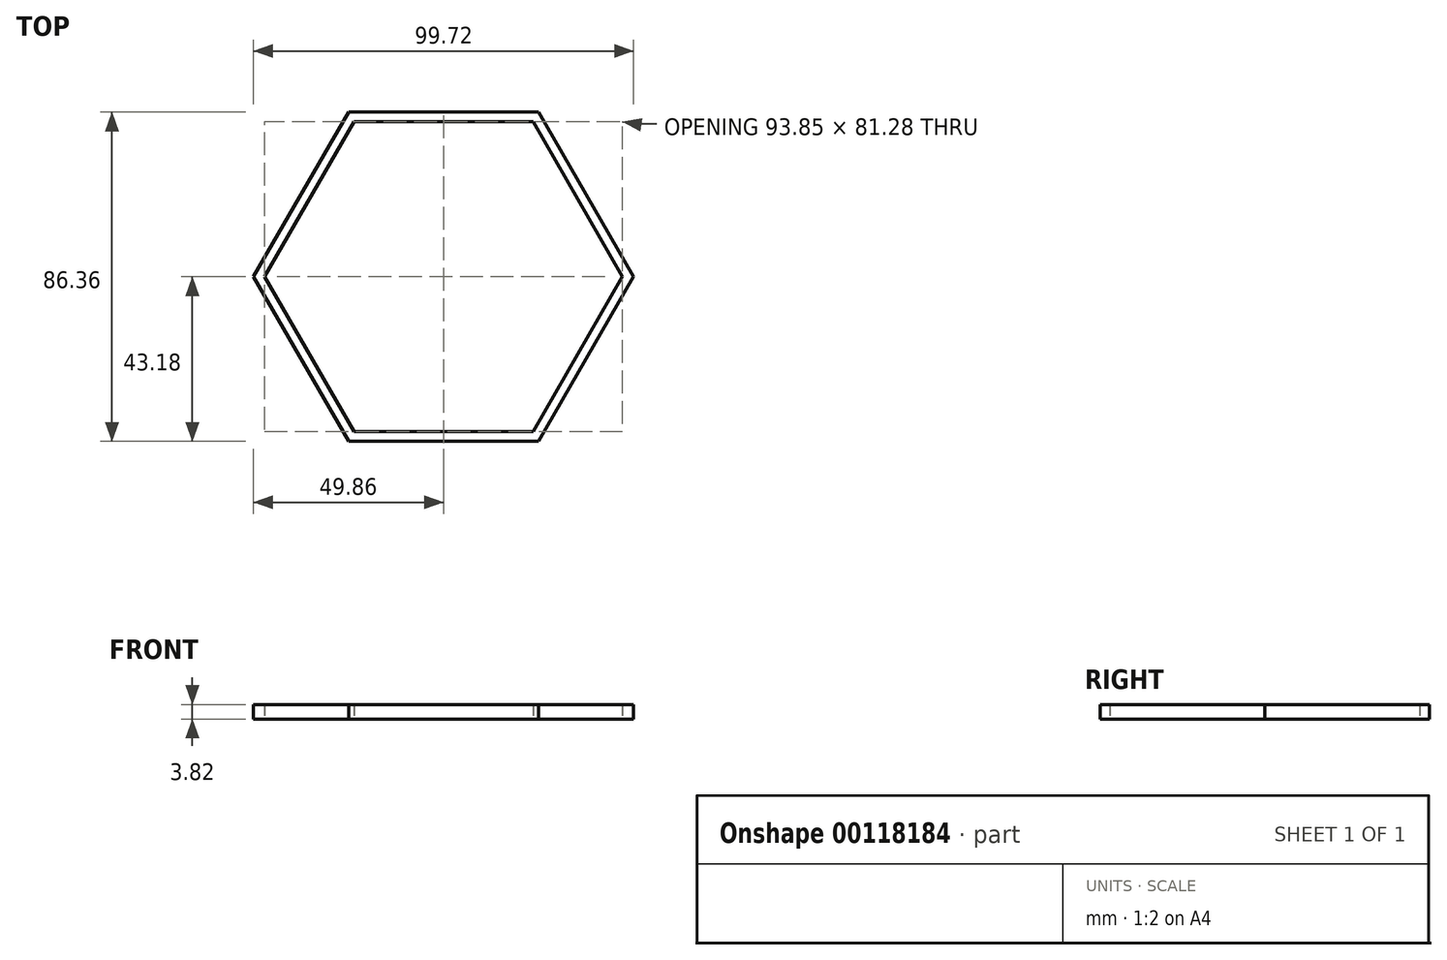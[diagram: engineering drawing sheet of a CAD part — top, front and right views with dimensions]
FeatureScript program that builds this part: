
annotation { "Feature Type Name" : "Feature", "Feature Type Description" : "" }
export const myFeature = defineFeature(function(context is Context, id is Id, definition is map)
    precondition{}
    {
        {
            var Q0;
            Q0=qCreatedBy(makeId("Top.planeOp"),FACE);
            var sketch = newSketch(context, id + "F0", { "sketchPlane" : qUnion([Q0])});
            skCircle(sketch, "E0.cCircle", {"center": v(0, 0) * mm, "radius": 40.64 * mm, "construction": true});
            skLineSegment(sketch, "E0.0", {"start": v(-23.46, 40.64) * mm, "end": v(23.46, 40.64) * mm});
            skLineSegment(sketch, "E0.1", {"start": v(23.46, 40.64) * mm, "end": v(46.93, 0) * mm});
            skLineSegment(sketch, "E0.2", {"start": v(46.93, 0) * mm, "end": v(23.46, -40.64) * mm});
            skLineSegment(sketch, "E0.3", {"start": v(23.46, -40.64) * mm, "end": v(-23.46, -40.64) * mm});
            skLineSegment(sketch, "E0.4", {"start": v(-23.46, -40.64) * mm, "end": v(-46.93, 0) * mm});
            skLineSegment(sketch, "E0.5", {"start": v(-46.93, 0) * mm, "end": v(-23.46, 40.64) * mm});
            skPoint(sketch, "E0.0.midPoint", {"position": v(0, 40.64) * mm});
            skLineSegment(sketch, "E1.0", {"start": v(-24.93, -43.18) * mm, "end": v(-49.86, 0) * mm});
            skLineSegment(sketch, "E1.1", {"start": v(-24.93, 43.18) * mm, "end": v(24.93, 43.18) * mm});
            skLineSegment(sketch, "E1.2", {"start": v(24.93, 43.18) * mm, "end": v(49.86, 0) * mm});
            skLineSegment(sketch, "E1.3", {"start": v(-49.86, 0) * mm, "end": v(-24.93, 43.18) * mm});
            skLineSegment(sketch, "E1.4", {"start": v(49.86, 0) * mm, "end": v(24.93, -43.18) * mm});
            skLineSegment(sketch, "E1.5", {"start": v(24.93, -43.18) * mm, "end": v(-24.93, -43.18) * mm});
            skSolve(sketch);
        }
        {
            var Q0;
            Q0=makeQuery(id+"F0.imprint","IMPRINT",FACE,{"disambiguationData":[TD([[makeQuery(id+"F0.imprint","IMPRINT",EDGE,{"derivedFrom":sQuery(id+"F0.wireOp",EDGE,"E0.0")}),1.0]])]});
            extrude(context, id + "F1", {"entities" : qUnion([Q0]), "endBound" : BoundingType.SYMMETRIC, "depth" : 3.8 * mm});
        }
    });
